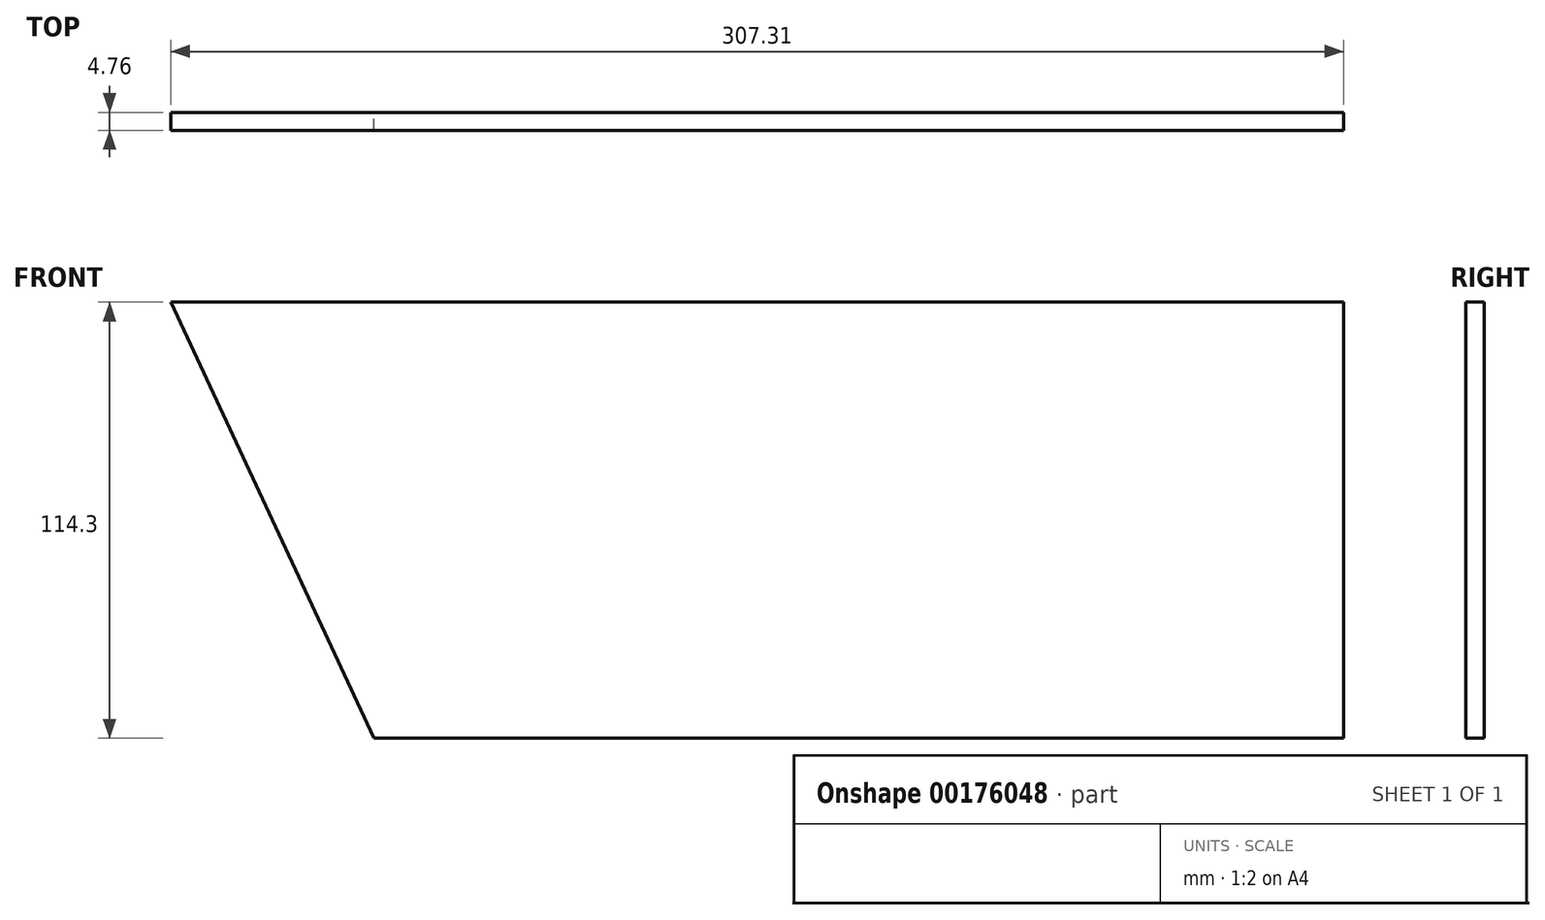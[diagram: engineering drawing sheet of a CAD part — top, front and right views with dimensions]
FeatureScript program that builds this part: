
annotation { "Feature Type Name" : "Feature", "Feature Type Description" : "" }
export const myFeature = defineFeature(function(context is Context, id is Id, definition is map)
    precondition{}
    {
        {
            var Q0;
            Q0=qCreatedBy(makeId("Front.planeOp"),FACE);
            var sketch = newSketch(context, id + "F0", { "sketchPlane" : qUnion([Q0])});
            skLineSegment(sketch, "E0", {"start": v(215.3, 82.21) * mm, "end": v(215.3, -32.09) * mm});
            skLineSegment(sketch, "E1", {"start": v(215.3, -32.09) * mm, "end": v(-38.7, -32.09) * mm});
            skLineSegment(sketch, "E2", {"start": v(-38.7, -32.09) * mm, "end": v(-92.02, 82.21) * mm});
            skLineSegment(sketch, "E3", {"start": v(-92.02, 82.21) * mm, "end": v(215.3, 82.21) * mm});
            skSolve(sketch);
        }
        {
            var Q0;
            Q0=makeQuery(id+"F0.imprint","IMPRINT",FACE,{"disambiguationData":[TD([[makeQuery(id+"F0.imprint","IMPRINT",EDGE,{"derivedFrom":sQuery(id+"F0.wireOp",EDGE,"E0")}),-1.0]])]});
            extrude(context, id + "F1", {"entities" : qUnion([Q0]), "depth" : 4.76 * mm});
        }
    });
